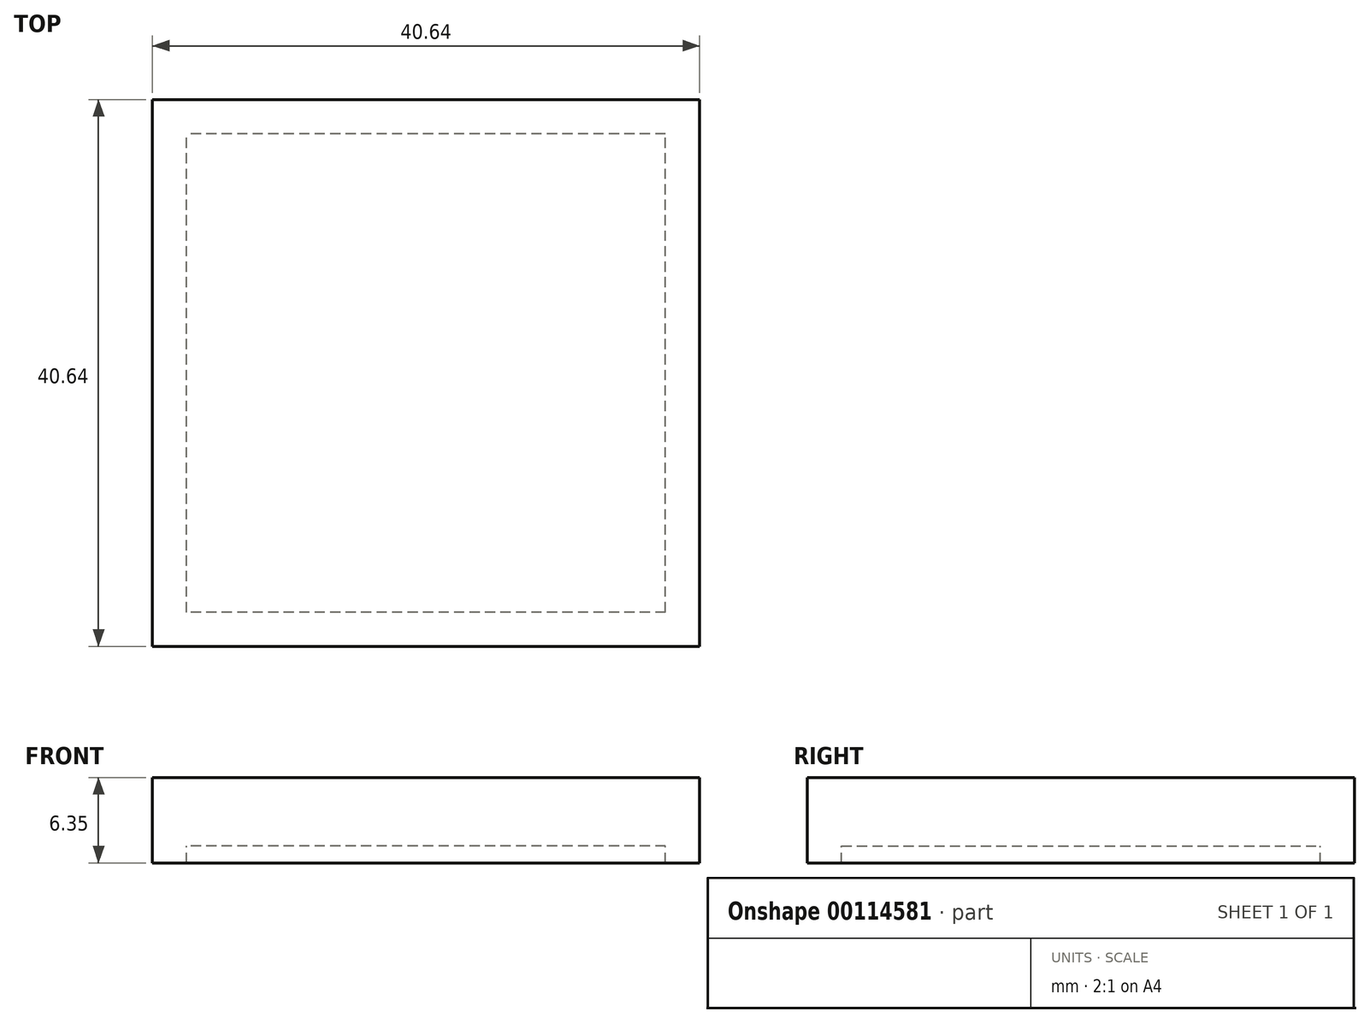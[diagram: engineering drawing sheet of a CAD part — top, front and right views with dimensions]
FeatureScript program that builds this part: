
annotation { "Feature Type Name" : "Feature", "Feature Type Description" : "" }
export const myFeature = defineFeature(function(context is Context, id is Id, definition is map)
    precondition{}
    {
        {
            var Q0;
            Q0=qCreatedBy(makeId("Top.planeOp"),FACE);
            var sketch = newSketch(context, id + "F0", { "sketchPlane" : qUnion([Q0])});
            skLineSegment(sketch, "E0.bottom", {"start": v(20.32, -20.32) * mm, "end": v(-20.32, -20.32) * mm});
            skLineSegment(sketch, "E0.top", {"start": v(20.32, 20.32) * mm, "end": v(-20.32, 20.32) * mm});
            skLineSegment(sketch, "E0.left", {"start": v(20.32, -20.32) * mm, "end": v(20.32, 20.32) * mm});
            skLineSegment(sketch, "E0.right", {"start": v(-20.32, -20.32) * mm, "end": v(-20.32, 20.32) * mm});
            skPoint(sketch, "E0.middle", {"position": v(0, 0) * mm});
            skLineSegment(sketch, "E1.bottom", {"start": v(17.78, -17.78) * mm, "end": v(-17.78, -17.78) * mm});
            skLineSegment(sketch, "E1.top", {"start": v(17.78, 17.78) * mm, "end": v(-17.78, 17.78) * mm});
            skLineSegment(sketch, "E1.left", {"start": v(17.78, -17.78) * mm, "end": v(17.78, 17.78) * mm});
            skLineSegment(sketch, "E1.right", {"start": v(-17.78, -17.78) * mm, "end": v(-17.78, 17.78) * mm});
            skSolve(sketch);
        }
        {
            var Q0;
            Q0=qSketchRegion(id+"F0",true);
            extrude(context, id + "F1", {"entities" : qUnion([Q0]), "oppositeDirection" : true, "depth" : 1.27 * mm});
        }
        {
            var Q0;
            Q0=qCreatedBy(makeId("Top.planeOp"),FACE);
            var sketch = newSketch(context, id + "F2", { "sketchPlane" : qUnion([Q0])});
            skLineSegment(sketch, "E2.bottom", {"start": v(20.32, 20.32) * mm, "end": v(-20.32, 20.32) * mm});
            skLineSegment(sketch, "E2.top", {"start": v(20.32, -20.32) * mm, "end": v(-20.32, -20.32) * mm});
            skLineSegment(sketch, "E2.left", {"start": v(20.32, 20.32) * mm, "end": v(20.32, -20.32) * mm});
            skLineSegment(sketch, "E2.right", {"start": v(-20.32, 20.32) * mm, "end": v(-20.32, -20.32) * mm});
            skPoint(sketch, "E2.middle", {"position": v(0, 0) * mm});
            skSolve(sketch);
        }
        {
            var Q0;
            Q0=qSketchRegion(id+"F2",true);
            extrude(context, id + "F3", {"entities" : qUnion([Q0]), "operationType" : NewBodyOperationType.ADD, "depth" : 5.08 * mm});
        }
    });
